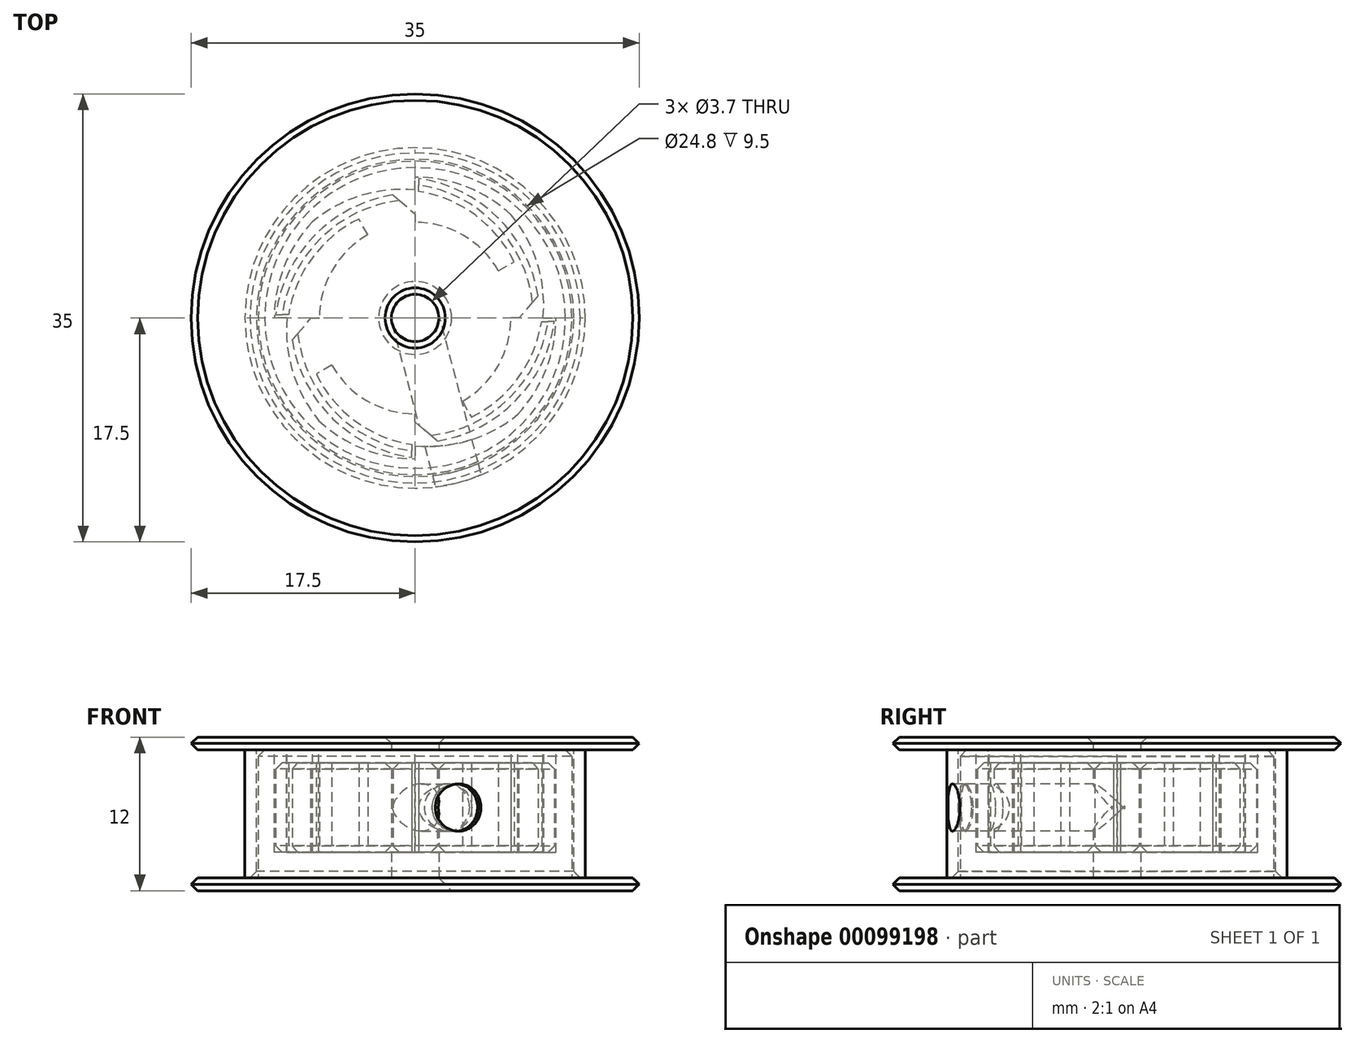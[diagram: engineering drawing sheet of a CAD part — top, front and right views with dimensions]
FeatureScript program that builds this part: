
annotation { "Feature Type Name" : "Feature", "Feature Type Description" : "" }
export const myFeature = defineFeature(function(context is Context, id is Id, definition is map)
    precondition{}
    {
        {
            var Q0;
            Q0=qCreatedBy(makeId("Top.planeOp"),FACE);
            var sketch = newSketch(context, id + "F0", { "sketchPlane" : qUnion([Q0])});
            skCircle(sketch, "E0", {"center": v(0, 0) * mm, "radius": 12.25 * mm});
            skCircle(sketch, "E1", {"center": v(0, 0) * mm, "radius": 1.85 * mm});
            skCircle(sketch, "E2", {"center": v(0, 0) * mm, "radius": 17.5 * mm});
            skSolve(sketch);
        }
        {
            var Q0;
            Q0=makeQuery(id+"F0.imprint","IMPRINT",FACE,{"disambiguationData":[TD([[makeQuery(id+"F0.imprint","IMPRINT",EDGE,{"derivedFrom":sQuery(id+"F0.wireOp",EDGE,"E0")}),1.0]])]});
            extrude(context, id + "F1", {"entities" : qUnion([Q0]), "depth" : 10 * mm});
        }
        {
            var Q0;
            Q0=makeQuery(id+"F0.imprint","IMPRINT",FACE,{"disambiguationData":[TD([[makeQuery(id+"F0.imprint","IMPRINT",EDGE,{"derivedFrom":sQuery(id+"F0.wireOp",EDGE,"E0")}),-1.0]])]});
            var Q1;
            Q1=makeQuery(id+"F0.imprint","IMPRINT",FACE,{"disambiguationData":[TD([[makeQuery(id+"F0.imprint","IMPRINT",EDGE,{"derivedFrom":sQuery(id+"F0.wireOp",EDGE,"E0")}),1.0]])]});
            extrude(context, id + "F2", {"entities" : qUnion([Q0, Q1]), "operationType" : NewBodyOperationType.ADD, "oppositeDirection" : true, "depth" : 1 * mm});
        }
        {
            var Q0;
            Q0=makeQuery(id+"F1.opExtrude","CAP_FACE",FACE,{"disambiguationData":[OSD([sQuery(id+"F0.wireOp",EDGE,"E0"),sQuery(id+"F0.wireOp",EDGE,"E1")])],"isStart":false});
            var sketch = newSketch(context, id + "F3", { "sketchPlane" : qUnion([Q0])});
            skCircle(sketch, "E3.0", {"center": v(0, 0) * mm, "radius": 17.5 * mm});
            skCircle(sketch, "E4.0", {"center": v(0, 0) * mm, "radius": 1.85 * mm});
            skCircle(sketch, "E5", {"center": v(0, 0) * mm, "radius": 9.5 * mm});
            skArc(sketch, "E6", {"start": v(-7.52, -8.02) * mm, "mid": v(-4.05, -10.23) * mm, "end": v(0, -11) * mm});
            skLineSegment(sketch, "E7", {"start": v(0, 10) * mm, "end": v(0, 11) * mm});
            skLineSegment(sketch, "E8", {"start": v(0, 0) * mm, "end": v(0, -1) * mm, "construction": true});
            skLineSegment(sketch, "E9", {"start": v(0, -1) * mm, "end": v(-1, -1) * mm, "construction": true});
            skArc(sketch, "E10.trimOffspring", {"start": v(0, 10) * mm, "mid": v(-4.26, 9.55) * mm, "end": v(-8.02, 7.52) * mm});
            skArc(sketch, "E11.1.0", {"start": v(-10, 0) * mm, "mid": v(-9.55, -4.26) * mm, "end": v(-7.52, -8.02) * mm});
            skLineSegment(sketch, "E11.1.1", {"start": v(-10, 0) * mm, "end": v(-11, 0) * mm});
            skArc(sketch, "E11.2.0", {"start": v(0, -10) * mm, "mid": v(4.26, -9.55) * mm, "end": v(8.02, -7.52) * mm});
            skLineSegment(sketch, "E11.2.1", {"start": v(0, -10) * mm, "end": v(0, -11) * mm});
            skArc(sketch, "E11.3.0", {"start": v(10, 0) * mm, "mid": v(9.55, 4.26) * mm, "end": v(7.52, 8.02) * mm});
            skLineSegment(sketch, "E11.3.1", {"start": v(10, 0) * mm, "end": v(11, 0) * mm});
            skArc(sketch, "E12.trimOffspring", {"start": v(-8.02, 7.52) * mm, "mid": v(-10.23, 4.05) * mm, "end": v(-11, 0) * mm});
            skArc(sketch, "E13.trimOffspring", {"start": v(7.52, 8.02) * mm, "mid": v(4.05, 10.23) * mm, "end": v(0, 11) * mm});
            skArc(sketch, "E14.trimOffspring", {"start": v(8.02, -7.52) * mm, "mid": v(10.23, -4.05) * mm, "end": v(11, 0) * mm});
            skSolve(sketch);
        }
        {
            var Q0;
            Q0=makeQuery(id+"FFGBfee8mG85BMw_1.opExtrude","CAP_EDGE",EDGE,{"disambiguationData":[OSD([sQuery(id+"F3.wireOp",EDGE,"E3.0")])],"isStart":false});
            var Q1;
            Q1=makeQuery(id+"F2.opExtrude","CAP_EDGE",EDGE,{"disambiguationData":[OSD([sQuery(id+"F0.wireOp",EDGE,"E2")])],"isStart":true});
            var Q2;
            Q2=makeQuery(id+"F2.opExtrude","CAP_EDGE",EDGE,{"disambiguationData":[OSD([sQuery(id+"F0.wireOp",EDGE,"E2")])],"isStart":false});
            var Q3;
            Q3=makeQuery(id+"FFGBfee8mG85BMw_1.opExtrude","CAP_EDGE",EDGE,{"disambiguationData":[OSD([sQuery(id+"F3.wireOp",EDGE,"E3.0")])],"isStart":true});
            chamfer(context, id + "F4", {"entities" : qUnion([Q0, Q1, Q2, Q3]), "width" : .5 * mm, "tangentPropagation" : true});
        }
        {
            var Q0;
            Q0=makeQuery(id+"F2.opExtrude","CAP_EDGE",EDGE,{"disambiguationData":[OSD([sQuery(id+"F0.wireOp",EDGE,"E1")])],"isStart":false});
            var Q1;
            Q1=makeQuery(id+"FFGBfee8mG85BMw_1.opExtrude","CAP_EDGE",EDGE,{"disambiguationData":[OSD([sQuery(id+"F3.wireOp",EDGE,"E4.0")])],"isStart":false});
            chamfer(context, id + "F5", {"entities" : qUnion([Q0, Q1]), "width" : 1 * mm, "tangentPropagation" : true});
        }
        {
            var Q0;
            Q0=makeQuery(id+"F3.imprint","IMPRINT",FACE,{"disambiguationData":[TD([[makeQuery(id+"F3.imprint","IMPRINT",EDGE,{"derivedFrom":sQuery(id+"F3.wireOp",EDGE,"E5")}),-1.0]])]});
            var Q1;
            Q1=makeQuery(id+"F3.imprint","IMPRINT",FACE,{"disambiguationData":[TD([[makeQuery(id+"F3.imprint","IMPRINT",EDGE,{"derivedFrom":sQuery(id+"F3.wireOp",EDGE,"E4.0")}),-1.0]])]});
            extrude(context, id + "F6", {"entities" : qUnion([Q0, Q1]), "operationType" : NewBodyOperationType.REMOVE, "oppositeDirection" : true, "depth" : 8 * mm});
        }
        {
            var Q0;
            Q0=makeQuery(id+"F6.boolean.opBoolean","COPY",FACE,{"derivedFrom":makeQuery(id+"F6.opExtrude","CAP_FACE",FACE,{"disambiguationData":[OSD([sQuery(id+"F3.wireOp",EDGE,"E4.0"),sQuery(id+"F3.wireOp",EDGE,"E6"),sQuery(id+"F3.wireOp",EDGE,"E7"),sQuery(id+"F3.wireOp",EDGE,"E10.trimOffspring"),sQuery(id+"F3.wireOp",EDGE,"E11.1.0"),sQuery(id+"F3.wireOp",EDGE,"E11.1.1"),sQuery(id+"F3.wireOp",EDGE,"E11.2.0"),sQuery(id+"F3.wireOp",EDGE,"E11.2.1"),sQuery(id+"F3.wireOp",EDGE,"E11.3.0"),sQuery(id+"F3.wireOp",EDGE,"E11.3.1"),sQuery(id+"F3.wireOp",EDGE,"E12.trimOffspring"),sQuery(id+"F3.wireOp",EDGE,"E13.trimOffspring"),sQuery(id+"F3.wireOp",EDGE,"E14.trimOffspring")])],"isStart":false})});
            var sketch = newSketch(context, id + "F7", { "sketchPlane" : qUnion([Q0])});
            skLineSegment(sketch, "E15", {"start": v(0, 0) * mm, "end": v(0, 1) * mm, "construction": true});
            skLineSegment(sketch, "E16", {"start": v(0, 1) * mm, "end": v(-0.5, 1) * mm, "construction": true});
            skLineSegment(sketch, "E17", {"start": v(-0.5, 1) * mm, "end": v(-0.5, 3.06) * mm, "construction": true});
            skLineSegment(sketch, "E18", {"start": v(0, 0) * mm, "end": v(-1.25, 0) * mm});
            skArc(sketch, "E19", {"start": v(9.75, 0) * mm, "mid": v(7.05, 7.22) * mm, "end": v(0.27, 10.9) * mm});
            skLineSegment(sketch, "E20", {"start": v(-0.5, 1) * mm, "end": v(-1.25, 1) * mm});
            skLineSegment(sketch, "E21", {"start": v(0, 9.75) * mm, "end": v(0, 7.48) * mm});
            skPoint(sketch, "E22.center", {"position": v(0, 0) * mm});
            skArc(sketch, "E23", {"start": v(7.73, 4.4) * mm, "mid": v(4.68, 8.05) * mm, "end": v(0.27, 9.88) * mm});
            skArc(sketch, "E24", {"start": v(6.5, 3.7) * mm, "mid": v(3.76, 6.47) * mm, "end": v(0, 7.48) * mm});
            skLineSegment(sketch, "E25", {"start": v(0.27, 9.88) * mm, "end": v(0.27, 10.9) * mm});
            skLineSegment(sketch, "E26", {"start": v(6.5, 3.7) * mm, "end": v(7.73, 4.4) * mm});
            skPoint(sketch, "E27.start.orphan", {"position": v(7.48, 0) * mm});
            skArc(sketch, "E28.1.0", {"start": v(0, 9.75) * mm, "mid": v(-7.22, 7.05) * mm, "end": v(-10.9, 0.27) * mm});
            skArc(sketch, "E28.1.1", {"start": v(-3.7, 6.5) * mm, "mid": v(-6.47, 3.76) * mm, "end": v(-7.48, 0) * mm});
            skLineSegment(sketch, "E28.1.2", {"start": v(-9.75, 0) * mm, "end": v(-7.48, 0) * mm});
            skArc(sketch, "E28.1.3", {"start": v(-4.4, 7.73) * mm, "mid": v(-8.05, 4.68) * mm, "end": v(-9.88, 0.27) * mm});
            skLineSegment(sketch, "E28.1.4", {"start": v(-9.88, 0.27) * mm, "end": v(-10.9, 0.27) * mm});
            skLineSegment(sketch, "E28.1.5", {"start": v(-3.7, 6.5) * mm, "end": v(-4.4, 7.73) * mm});
            skPoint(sketch, "E28.1.6", {"position": v(0, 7.48) * mm});
            skArc(sketch, "E28.2.0", {"start": v(-9.75, 0) * mm, "mid": v(-7.05, -7.22) * mm, "end": v(-0.27, -10.9) * mm});
            skArc(sketch, "E28.2.1", {"start": v(-6.5, -3.7) * mm, "mid": v(-3.76, -6.47) * mm, "end": v(0, -7.48) * mm});
            skLineSegment(sketch, "E28.2.2", {"start": v(0, -9.75) * mm, "end": v(0, -7.48) * mm});
            skArc(sketch, "E28.2.3", {"start": v(-7.73, -4.4) * mm, "mid": v(-4.68, -8.05) * mm, "end": v(-0.27, -9.88) * mm});
            skLineSegment(sketch, "E28.2.4", {"start": v(-0.27, -9.88) * mm, "end": v(-0.27, -10.9) * mm});
            skLineSegment(sketch, "E28.2.5", {"start": v(-6.5, -3.7) * mm, "end": v(-7.73, -4.4) * mm});
            skPoint(sketch, "E28.2.6", {"position": v(-7.48, 0) * mm});
            skArc(sketch, "E28.3.0", {"start": v(0, -9.75) * mm, "mid": v(7.22, -7.05) * mm, "end": v(10.9, -0.27) * mm});
            skArc(sketch, "E28.3.1", {"start": v(3.7, -6.5) * mm, "mid": v(6.47, -3.76) * mm, "end": v(7.48, 0) * mm});
            skLineSegment(sketch, "E28.3.2", {"start": v(9.75, 0) * mm, "end": v(7.48, 0) * mm});
            skArc(sketch, "E28.3.3", {"start": v(4.4, -7.73) * mm, "mid": v(8.05, -4.68) * mm, "end": v(9.88, -0.27) * mm});
            skLineSegment(sketch, "E28.3.4", {"start": v(9.88, -0.27) * mm, "end": v(10.9, -0.27) * mm});
            skLineSegment(sketch, "E28.3.5", {"start": v(3.7, -6.5) * mm, "end": v(4.4, -7.73) * mm});
            skPoint(sketch, "E28.3.6", {"position": v(0, -7.48) * mm});
            skPoint(sketch, "E29.orphan", {"position": v(0, 8.75) * mm});
            skPoint(sketch, "E30.orphan", {"position": v(0, -8.75) * mm});
            skPoint(sketch, "E31.orphan", {"position": v(-8.75, 0) * mm});
            skPoint(sketch, "E32.orphan", {"position": v(8.75, 0) * mm});
            skCircle(sketch, "E33", {"center": v(0, 0) * mm, "radius": 1.75 * mm});
            skLineSegment(sketch, "E34", {"start": v(0, -7.48) * mm, "end": v(3.7, -6.5) * mm, "construction": true});
            skSolve(sketch);
        }
        {
            var Q0;
            Q0=makeQuery(id+"F7.imprint","IMPRINT",FACE,{"disambiguationData":[TD([[makeQuery(id+"F7.imprint","IMPRINT",EDGE,{"derivedFrom":sQuery(id+"F7.wireOp",EDGE,"E19")}),1.0]])]});
            extrude(context, id + "F8", {"entities" : qUnion([Q0]), "depth" : 7 * mm});
        }
        {
            var Q0;
            Q0=makeQuery(id+"F8.opExtrude","CAP_EDGE",EDGE,{"disambiguationData":[OSD([sQuery(id+"F7.wireOp",EDGE,"E28.1.0")])],"isStart":false});
            var Q1;
            Q1=makeQuery(id+"F8.opExtrude","CAP_EDGE",EDGE,{"disambiguationData":[OSD([sQuery(id+"F7.wireOp",EDGE,"E19")])],"isStart":false});
            var Q2;
            Q2=makeQuery(id+"F8.opExtrude","CAP_EDGE",EDGE,{"disambiguationData":[OSD([sQuery(id+"F7.wireOp",EDGE,"E28.3.0")])],"isStart":false});
            var Q3;
            Q3=makeQuery(id+"F8.opExtrude","CAP_EDGE",EDGE,{"disambiguationData":[OSD([sQuery(id+"F7.wireOp",EDGE,"E28.2.0")])],"isStart":false});
            var Q4;
            Q4=makeQuery(id+"F8.opExtrude","CAP_EDGE",EDGE,{"disambiguationData":[OSD([sQuery(id+"F7.wireOp",EDGE,"E28.1.0")])],"isStart":true});
            var Q5;
            Q5=makeQuery(id+"F8.opExtrude","CAP_EDGE",EDGE,{"disambiguationData":[OSD([sQuery(id+"F7.wireOp",EDGE,"E19")])],"isStart":true});
            var Q6;
            Q6=makeQuery(id+"F8.opExtrude","CAP_EDGE",EDGE,{"disambiguationData":[OSD([sQuery(id+"F7.wireOp",EDGE,"E28.3.0")])],"isStart":true});
            var Q7;
            Q7=makeQuery(id+"F8.opExtrude","CAP_EDGE",EDGE,{"disambiguationData":[OSD([sQuery(id+"F7.wireOp",EDGE,"E28.2.0")])],"isStart":true});
            var Q8;
            Q8=makeQuery(id+"F8.opExtrude","CAP_EDGE",EDGE,{"disambiguationData":[OSD([sQuery(id+"F3.wireOp",EDGE,"E4.0")])],"isStart":false});
            var Q9;
            Q9=makeQuery(id+"F8.opExtrude","CAP_EDGE",EDGE,{"disambiguationData":[OSD([sQuery(id+"F3.wireOp",EDGE,"E4.0")])],"isStart":true});
            chamfer(context, id + "F9", {"entities" : qUnion([Q0, Q1, Q2, Q3, Q4, Q5, Q6, Q7, Q8, Q9]), "width" : .5 * mm, "tangentPropagation" : true});
        }
        {
            var Q0;
            Q0=sQuery(id+"F7.wireOp",EDGE,"E34");
            cPlane(context, id + "F10", {"entities" : qUnion([Q0]), "cplaneType" : CPlaneType.LINE_ANGLE, "offset" : 150 * mm, "angle" : 0 * degree, "width" : 150 * mm, "height" : 150 * mm});
        }
        {
            var Q0;
            Q0=makeQuery(id+"F8.opExtrude","SWEPT_EDGE",EDGE,{"disambiguationData":[OSD([sQuery(id+"F7.wireOp",EDGE,"E19"),sQuery(id+"F7.wireOp",EDGE,"E28.3.2")])]});
            var Q1;
            Q1=makeQuery(id+"F8.opExtrude","SWEPT_EDGE",EDGE,{"disambiguationData":[OSD([sQuery(id+"F7.wireOp",EDGE,"E28.2.2"),sQuery(id+"F7.wireOp",EDGE,"E28.3.0")])]});
            var Q2;
            Q2=makeQuery(id+"F8.opExtrude","SWEPT_EDGE",EDGE,{"disambiguationData":[OSD([sQuery(id+"F7.wireOp",EDGE,"E28.1.2"),sQuery(id+"F7.wireOp",EDGE,"E28.2.0")])]});
            var Q3;
            Q3=makeQuery(id+"F8.opExtrude","SWEPT_EDGE",EDGE,{"disambiguationData":[OSD([sQuery(id+"F7.wireOp",EDGE,"E21"),sQuery(id+"F7.wireOp",EDGE,"E28.1.0")])]});
            chamfer(context, id + "F11", {"entities" : qUnion([Q0, Q1, Q2, Q3]), "width" : 1.5 * mm, "tangentPropagation" : true});
        }
        {
            var Q0;
            Q0=makeQuery(id+"F1.opExtrude","CAP_FACE",FACE,{"disambiguationData":[OSD([sQuery(id+"F0.wireOp",EDGE,"E0"),sQuery(id+"F0.wireOp",EDGE,"E1")])],"isStart":false});
            var sketch = newSketch(context, id + "F12", { "sketchPlane" : qUnion([Q0])});
            skCircle(sketch, "E35.0", {"center": v(0, 0) * mm, "radius": 17.5 * mm});
            skCircle(sketch, "E36", {"center": v(0, 0) * mm, "radius": 12.4 * mm});
            skCircle(sketch, "E37", {"center": v(0, 0) * mm, "radius": 13.3 * mm});
            skCircle(sketch, "E38.0", {"center": v(0, 0) * mm, "radius": 1.85 * mm});
            skSolve(sketch);
        }
        {
            var Q0;
            Q0=makeQuery(id+"F12.imprint","IMPRINT",FACE,{"disambiguationData":[TD([[makeQuery(id+"F12.imprint","IMPRINT",EDGE,{"derivedFrom":sQuery(id+"F12.wireOp",EDGE,"E36")}),-1.0]])]});
            var Q1;
            Q1=makeQuery(id+"F2.opExtrude","CAP_FACE",FACE,{"disambiguationData":[OSD([sQuery(id+"F0.wireOp",EDGE,"E1"),sQuery(id+"F0.wireOp",EDGE,"E2")])],"isStart":true});
            extrude(context, id + "F13", {"entities" : qUnion([Q0]), "endBound" : BoundingType.UP_TO_SURFACE, "oppositeDirection" : true, "endBoundEntityFace" : qUnion([Q1]), "depth" : 8 * mm});
        }
        {
            var Q0;
            Q0=makeQuery(id+"F12.imprint","IMPRINT",FACE,{"disambiguationData":[TD([[makeQuery(id+"F12.imprint","IMPRINT",EDGE,{"derivedFrom":sQuery(id+"F12.wireOp",EDGE,"E36")}),1.0]])]});
            var Q1;
            Q1=makeQuery(id+"F12.imprint","IMPRINT",FACE,{"disambiguationData":[TD([[makeQuery(id+"F12.imprint","IMPRINT",EDGE,{"derivedFrom":makeQuery(id+"F1.opExtrude","CAP_EDGE",EDGE,{"disambiguationData":[OSD([sQuery(id+"F0.wireOp",EDGE,"E0")])],"isStart":false})}),1.0]])]});
            var Q2;
            Q2=makeQuery(id+"F12.imprint","IMPRINT",FACE,{"disambiguationData":[TD([[makeQuery(id+"F12.imprint","IMPRINT",EDGE,{"derivedFrom":sQuery(id+"F12.wireOp",EDGE,"E38.0")}),-1.0]])]});
            var Q3;
            Q3=makeQuery(id+"F12.imprint","IMPRINT",FACE,{"disambiguationData":[TD([[makeQuery(id+"F12.imprint","IMPRINT",EDGE,{"derivedFrom":sQuery(id+"F12.wireOp",EDGE,"E36")}),-1.0]])]});
            var Q4;
            Q4=makeQuery(id+"F12.imprint","IMPRINT",FACE,{"disambiguationData":[TD([[makeQuery(id+"F12.imprint","IMPRINT",EDGE,{"derivedFrom":sQuery(id+"F12.wireOp",EDGE,"E35.0")}),1.0]])]});
            extrude(context, id + "F14", {"entities" : qUnion([Q0, Q1, Q2, Q3, Q4]), "depth" : 1 * mm});
        }
        {
            var Q0;
            Q0=makeQuery(id+"F14.opExtrude","CAP_EDGE",EDGE,{"disambiguationData":[OSD([sQuery(id+"F12.wireOp",EDGE,"E35.0")])],"isStart":false});
            var Q1;
            Q1=makeQuery(id+"F14.opExtrude","CAP_EDGE",EDGE,{"disambiguationData":[OSD([sQuery(id+"F12.wireOp",EDGE,"E35.0")])],"isStart":true});
            var Q2;
            Q2=makeQuery(id+"F14.opExtrude","CAP_EDGE",EDGE,{"disambiguationData":[OSD([sQuery(id+"F12.wireOp",EDGE,"E38.0")])],"isStart":false});
            chamfer(context, id + "F15", {"entities" : qUnion([Q0, Q1, Q2]), "width" : .5 * mm, "tangentPropagation" : true});
        }
        {
            var Q0;
            Q0=qCreatedBy(id+"F10.planeOp",FACE);
            cPlane(context, id + "F16", {"entities" : qUnion([Q0]), "cplaneType" : CPlaneType.OFFSET, "offset" : 10 * mm, "oppositeDirection" : true, "width" : 150 * mm, "height" : 150 * mm});
        }
        {
            var Q0;
            Q0=qCreatedBy(id+"F16.planeOp",FACE);
            var sketch = newSketch(context, id + "F17", { "sketchPlane" : qUnion([Q0])});
            skLineSegment(sketch, "E39", {"start": v(0, 0) * mm, "end": v(0, 5.5) * mm, "construction": true});
            skCircle(sketch, "E40", {"center": v(0, 5.5) * mm, "radius": 1.85 * mm});
            skSolve(sketch);
        }
        {
            var Q0;
            Q0=makeQuery(id+"F17.imprint","IMPRINT",FACE,{"disambiguationData":[TD([[makeQuery(id+"F17.imprint","IMPRINT",EDGE,{"derivedFrom":sQuery(id+"F17.wireOp",EDGE,"E40")}),1.0]])]});
            extrude(context, id + "F18", {"entities" : qUnion([Q0]), "operationType" : NewBodyOperationType.REMOVE, "depth" : 17.35 * mm});
        }
        {
            var Q0;
            Q0=makeQuery(id+"F13.opExtrude","CAP_EDGE",EDGE,{"disambiguationData":[OSD([sQuery(id+"F12.wireOp",EDGE,"E36")])],"isStart":false});
            var Q1;
            Q1=makeQuery(id+"F1.opExtrude","CAP_EDGE",EDGE,{"disambiguationData":[OSD([sQuery(id+"F0.wireOp",EDGE,"E0")])],"isStart":false});
            chamfer(context, id + "F19", {"entities" : qUnion([Q0, Q1]), "width" : .5 * mm, "tangentPropagation" : true});
        }
    });
